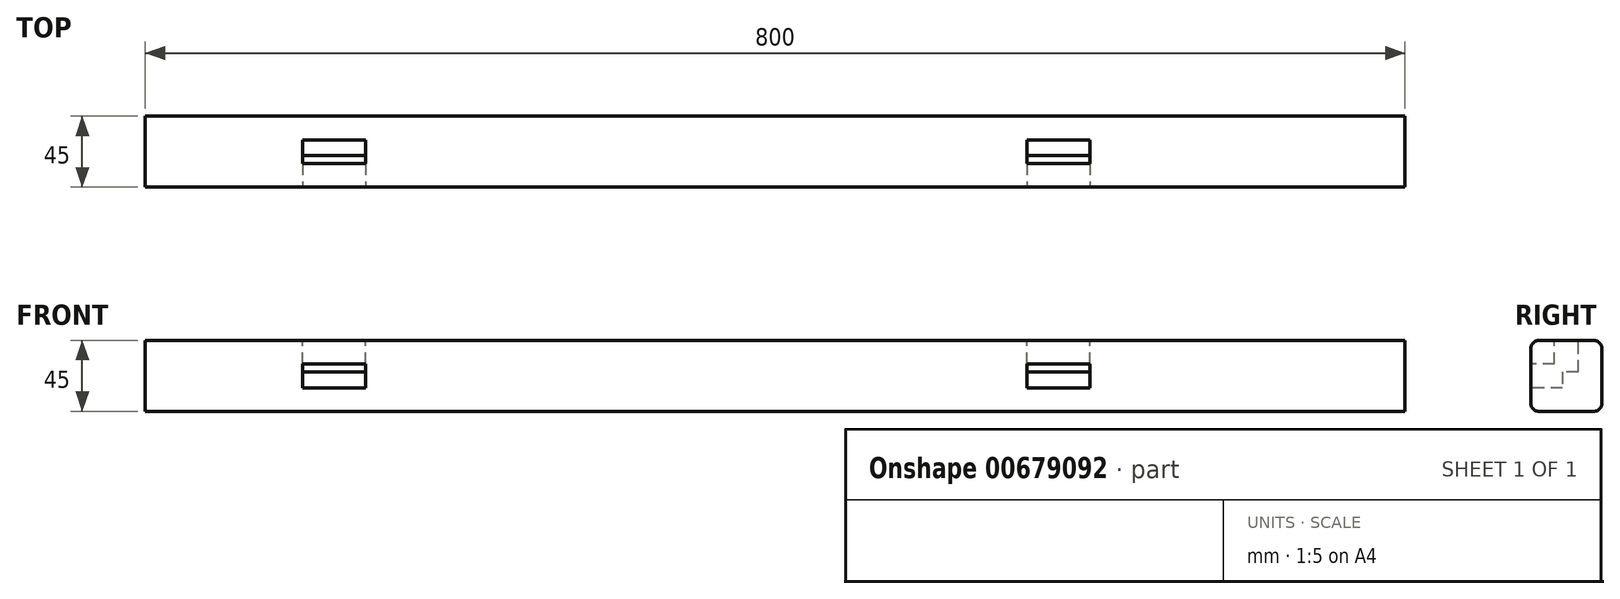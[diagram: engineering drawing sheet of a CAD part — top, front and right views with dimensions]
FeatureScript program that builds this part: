
annotation { "Feature Type Name" : "Feature", "Feature Type Description" : "" }
export const myFeature = defineFeature(function(context is Context, id is Id, definition is map)
    precondition{}
    {
        {
            var Q0;
            Q0=qCreatedBy(makeId("Right.planeOp"),FACE);
            var sketch = newSketch(context, id + "F0", { "sketchPlane" : qUnion([Q0])});
            skLineSegment(sketch, "E0.bottom", {"start": v(22.5, 22.5) * mm, "end": v(-22.5, 22.5) * mm});
            skLineSegment(sketch, "E0.top", {"start": v(22.5, -22.5) * mm, "end": v(-22.5, -22.5) * mm});
            skLineSegment(sketch, "E0.left", {"start": v(22.5, 22.5) * mm, "end": v(22.5, -22.5) * mm});
            skLineSegment(sketch, "E0.right", {"start": v(-22.5, 22.5) * mm, "end": v(-22.5, -22.5) * mm});
            skPoint(sketch, "E0.middle", {"position": v(0, 0) * mm});
            skSolve(sketch);
        }
        {
            var Q0;
            Q0 = qSketchRegion(id + "F0", true);
            extrude(context, id + "F1", {"entities" : qUnion([Q0]), "endBound" : BoundingType.SYMMETRIC, "depth" : 800 * mm, "offsetDistance" : 25 * mm});
        }
        {
            var Q0;
            Q0=makeQuery(id+"F1.opExtrude","SWEPT_EDGE",EDGE,{"disambiguationData":[OSD([sQuery(id+"F0.wireOp",EDGE,"E0.bottom"),sQuery(id+"F0.wireOp",EDGE,"E0.right")])]});
            var Q1;
            Q1=makeQuery(id+"F1.opExtrude","SWEPT_EDGE",EDGE,{"disambiguationData":[OSD([sQuery(id+"F0.wireOp",EDGE,"E0.bottom"),sQuery(id+"F0.wireOp",EDGE,"E0.left")])]});
            var Q2;
            Q2=makeQuery(id+"F1.opExtrude","SWEPT_EDGE",EDGE,{"disambiguationData":[OSD([sQuery(id+"F0.wireOp",EDGE,"E0.top"),sQuery(id+"F0.wireOp",EDGE,"E0.right")])]});
            var Q3;
            Q3=makeQuery(id+"F1.opExtrude","SWEPT_EDGE",EDGE,{"disambiguationData":[OSD([sQuery(id+"F0.wireOp",EDGE,"E0.top"),sQuery(id+"F0.wireOp",EDGE,"E0.left")])]});
            fillet(context, id + "F2", {"entities" : qUnion([Q0, Q1, Q2, Q3]), "radius" : 5 * mm, "tangentPropagation" : true, "allowEdgeOverflow" : false});
        }
        {
            var Q0;
            Q0=makeQuery(id+"F1.opExtrude","SWEPT_FACE",FACE,{"disambiguationData":[OSD([sQuery(id+"F0.wireOp",EDGE,"E0.bottom")])]});
            var sketch = newSketch(context, id + "F3", { "sketchPlane" : qUnion([Q0])});
            skLineSegment(sketch, "E1.bottom", {"start": v(-260, 7.5) * mm, "end": v(-300, 7.5) * mm});
            skLineSegment(sketch, "E1.top", {"start": v(-260, -7.5) * mm, "end": v(-300, -7.5) * mm});
            skLineSegment(sketch, "E1.left", {"start": v(-260, 7.5) * mm, "end": v(-260, -7.5) * mm});
            skLineSegment(sketch, "E1.right", {"start": v(-300, 7.5) * mm, "end": v(-300, -7.5) * mm});
            skPoint(sketch, "E1.middle", {"position": v(-280, 0) * mm});
            skSolve(sketch);
        }
        {
            var Q0;
            Q0 = qSketchRegion(id + "F3", true);
            extrude(context, id + "F4", {"entities" : qUnion([Q0]), "operationType" : NewBodyOperationType.REMOVE, "oppositeDirection" : true, "depth" : 20 * mm, "offsetDistance" : 25 * mm});
        }
        {
            var Q0;
            Q0=makeQuery(id+"F1.opExtrude","SWEPT_FACE",FACE,{"disambiguationData":[OSD([sQuery(id+"F0.wireOp",EDGE,"E0.right")])]});
            var sketch = newSketch(context, id + "F5", { "sketchPlane" : qUnion([Q0])});
            skLineSegment(sketch, "E2.bottom", {"start": v(-260, 7.5) * mm, "end": v(-300, 7.5) * mm});
            skLineSegment(sketch, "E2.top", {"start": v(-260, -7.5) * mm, "end": v(-300, -7.5) * mm});
            skLineSegment(sketch, "E2.left", {"start": v(-260, 7.5) * mm, "end": v(-260, -7.5) * mm});
            skLineSegment(sketch, "E2.right", {"start": v(-300, 7.5) * mm, "end": v(-300, -7.5) * mm});
            skPoint(sketch, "E2.middle", {"position": v(-280, 0) * mm});
            skSolve(sketch);
        }
        {
            var Q0;
            Q0 = qSketchRegion(id + "F5", true);
            extrude(context, id + "F6", {"entities" : qUnion([Q0]), "operationType" : NewBodyOperationType.REMOVE, "oppositeDirection" : true, "depth" : 20 * mm, "offsetDistance" : 25 * mm});
        }
        {
            var Q0;
            Q0=makeQuery(id+"F1.opExtrude","SWEPT_FACE",FACE,{"disambiguationData":[OSD([sQuery(id+"F0.wireOp",EDGE,"E0.bottom")])]});
            var sketch = newSketch(context, id + "F7", { "sketchPlane" : qUnion([Q0])});
            skLineSegment(sketch, "E3.bottom", {"start": v(160, 7.5) * mm, "end": v(200, 7.5) * mm});
            skLineSegment(sketch, "E3.top", {"start": v(160, -7.5) * mm, "end": v(200, -7.5) * mm});
            skLineSegment(sketch, "E3.left", {"start": v(160, 7.5) * mm, "end": v(160, -7.5) * mm});
            skLineSegment(sketch, "E3.right", {"start": v(200, 7.5) * mm, "end": v(200, -7.5) * mm});
            skPoint(sketch, "E3.middle", {"position": v(180, 0) * mm});
            skSolve(sketch);
        }
        {
            var Q0;
            Q0=makeQuery(id+"F7.imprint","IMPRINT",FACE,{"disambiguationData":[TD([[makeQuery(id+"F7.imprint","IMPRINT",EDGE,{"derivedFrom":sQuery(id+"F7.wireOp",EDGE,"E3.bottom")}),-1.0]])]});
            extrude(context, id + "F8", {"entities" : qUnion([Q0]), "operationType" : NewBodyOperationType.REMOVE, "oppositeDirection" : true, "depth" : 20 * mm, "offsetDistance" : 25 * mm});
        }
        {
            var Q0;
            Q0=makeQuery(id+"F1.opExtrude","SWEPT_FACE",FACE,{"disambiguationData":[OSD([sQuery(id+"F0.wireOp",EDGE,"E0.right")])]});
            var sketch = newSketch(context, id + "F9", { "sketchPlane" : qUnion([Q0])});
            skLineSegment(sketch, "E4.bottom", {"start": v(200, 7.5) * mm, "end": v(160, 7.5) * mm});
            skLineSegment(sketch, "E4.top", {"start": v(200, -7.5) * mm, "end": v(160, -7.5) * mm});
            skLineSegment(sketch, "E4.left", {"start": v(200, 7.5) * mm, "end": v(200, -7.5) * mm});
            skLineSegment(sketch, "E4.right", {"start": v(160, 7.5) * mm, "end": v(160, -7.5) * mm});
            skPoint(sketch, "E4.middle", {"position": v(180, 0) * mm});
            skSolve(sketch);
        }
        {
            var Q0;
            Q0 = qSketchRegion(id + "F9", true);
            extrude(context, id + "F10", {"entities" : qUnion([Q0]), "operationType" : NewBodyOperationType.REMOVE, "oppositeDirection" : true, "depth" : 20 * mm, "offsetDistance" : 25 * mm});
        }
    });
